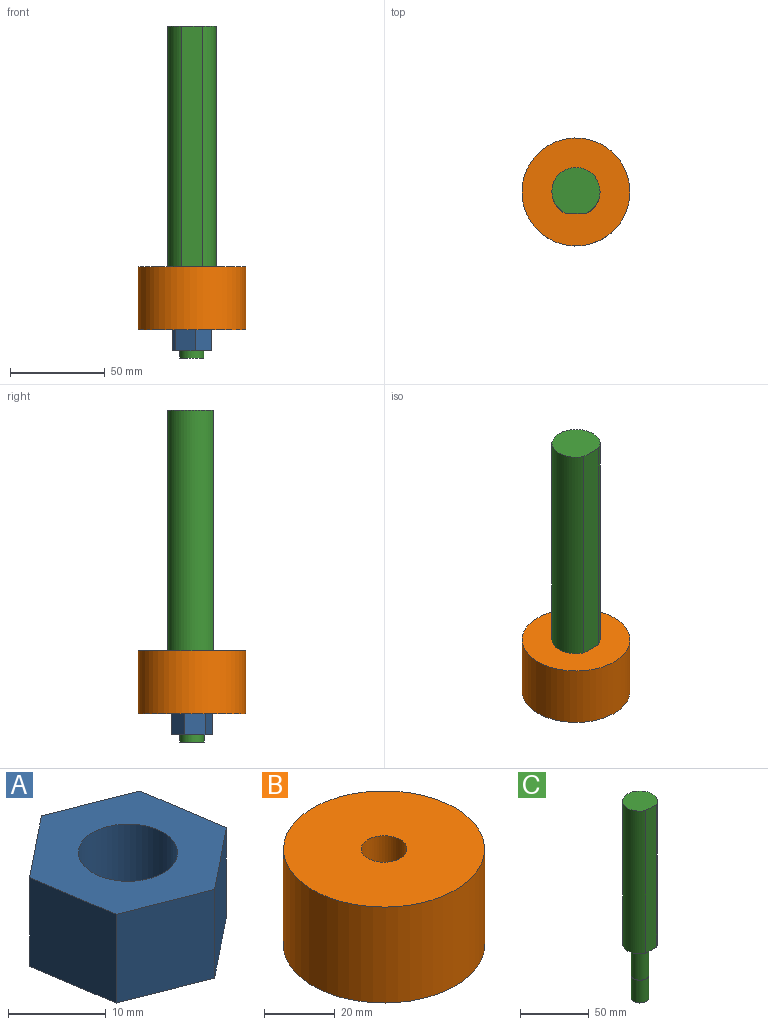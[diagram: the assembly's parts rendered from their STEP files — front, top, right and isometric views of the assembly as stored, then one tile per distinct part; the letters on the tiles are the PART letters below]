
ASSEMBLY  parts=3 mates=4
PART A: 9 faces, bbox 20.5x21.7x11.1 mm
  f0: plane 11.11x10.87mm, normal (0.99,0.15,0), area 122.2mm2, adj f1,f6,f7,f8
  f1: plane 11.11x10.24mm, normal (0.36,0.93,0), area 122.2mm2, adj f0,f2,f7,f8
  f2: plane 11.11x8.59mm, normal (-0.62,0.78,0), area 122.2mm2, adj f1,f3,f7,f8
  f3: plane 11.11x10.87mm, normal (-0.99,-0.15,0), area 122.2mm2, adj f2,f4,f7,f8
  f4: plane 11.11x10.24mm, normal (-0.36,-0.93,0), area 122.2mm2, adj f3,f6,f7,f8
  f5: cylinder r=5.08mm len=11.11mm, axis (0,0,-1), area 354.7mm2, adj f7,f8
  f6: plane 11.11x8.59mm, normal (0.62,-0.78,0), area 122.2mm2, adj f0,f4,f7,f8
  f7: plane 21.75x20.49mm, normal (0,0,1), area 233.2mm2, adj f0,f1,f2,f3,f4,f5,f6
  f8: plane 21.75x20.49mm, normal (0,0,-1), area 233.2mm2, adj f0,f1,f2,f3,f4,f5,f6
PART B: 4 faces, bbox 57x57x33.3 mm
  f0: cylinder r=6.49mm len=33.27mm, axis (0,0,-1), area 1356.8mm2, adj f2,f3
  f1: cylinder r=28.5mm len=57mm, axis (0,0,-1), area 5958.2mm2, adj f2,f3
  f2: plane 57x57mm, normal (0,0,1), area 2419.2mm2, adj f0,f1
  f3: plane 57x57mm, normal (0,0,-1), area 2419.2mm2, adj f0,f1
PART C: 8 faces, bbox 25.4x24.1x175.3 mm
  f0: plane 25.4x24.13mm, normal (0,0,-1), area 365.4mm2, adj f5,f6,f7
  f1: plane 25.4x24.13mm, normal (0,0,1), area 497.2mm2, adj f6,f7
  f2: plane 12.7x12.7mm, normal (0,0,-1), area 126.7mm2, adj f3
  f3: cylinder r=6.35mm len=20.32mm, axis (0,0,-1), area 810.7mm2, adj f2,f4
  f4: plane 12.95x12.95mm, normal (0,0,-1), area 5.1mm2, adj f3,f5
  f5: cylinder r=6.48mm len=27.94mm, axis (0,0,-1), area 1137.1mm2, adj f0,f4
  f6: cylinder r=12.7mm len=127mm, axis (0,0,-1), area 8679.2mm2, adj f0,f1,f7
  f7: plane 127x11.07mm, normal (0,-1,0), area 1406.1mm2, adj f0,f1,f6
PLACE A t=(-115.36,97.03,-2.09)mm
PLACE B t=(-190.07,16.63,9.02)mm
PLACE C t=(0.98,62.29,-5.96)mm
MATE slider C.f3 <-> B.f0  axis (0,0,-1) through (0.98,62.29,28.33)mm
MATE planar B.f0 <-> C.f0  axis (0,0,1) through (0.98,62.29,42.3)mm
MATE planar B.f0 <-> A.f7  axis (0,0,-1) through (0.98,62.29,9.02)mm
MATE slider C.f3 <-> A.f5  axis (0,0,-1) through (0.98,62.29,4.2)mm
